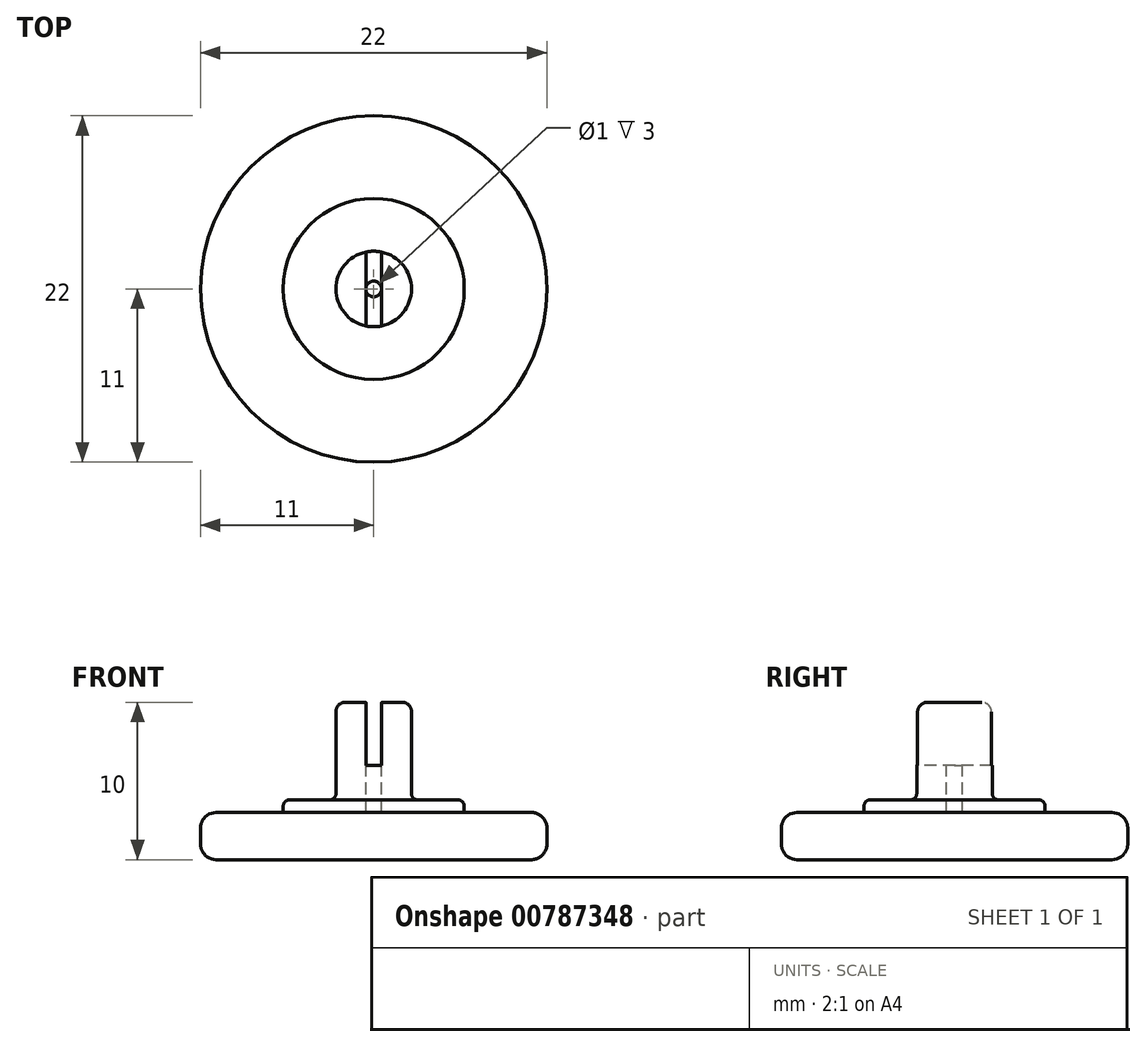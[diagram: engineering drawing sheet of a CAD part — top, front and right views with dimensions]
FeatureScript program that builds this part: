
annotation { "Feature Type Name" : "Feature", "Feature Type Description" : "" }
export const myFeature = defineFeature(function(context is Context, id is Id, definition is map)
    precondition{}
    {
        {
            var Q0;
            Q0=qCreatedBy(makeId("Top.planeOp"),FACE);
            var sketch = newSketch(context, id + "F0", { "sketchPlane" : qUnion([Q0])});
            skCircle(sketch, "E0", {"center": v(0, 0) * mm, "radius": 11 * mm});
            skSolve(sketch);
        }
        {
            var Q0;
            Q0=qSketchRegion(id+"F0",true);
            extrude(context, id + "F1", {"entities" : qUnion([Q0]), "depth" : 3 * mm});
        }
        {
            var Q0;
            Q0=makeQuery(id+"F1.opExtrude","CAP_FACE",FACE,{"disambiguationData":[OSD([sQuery(id+"F0.wireOp",EDGE,"E0")])],"isStart":false});
            var sketch = newSketch(context, id + "F2", { "sketchPlane" : qUnion([Q0])});
            skCircle(sketch, "E1", {"center": v(0, 0) * mm, "radius": 5.75 * mm});
            skSolve(sketch);
        }
        {
            var Q0;
            Q0=qSketchRegion(id+"F2",true);
            extrude(context, id + "F3", {"entities" : qUnion([Q0]), "operationType" : NewBodyOperationType.ADD, "depth" : .8 * mm, "offsetDistance" : 25 * mm});
        }
        {
            var Q0;
            Q0=makeQuery(id+"F3.opExtrude","CAP_FACE",FACE,{"disambiguationData":[OSD([sQuery(id+"F2.wireOp",EDGE,"E1")])],"isStart":false});
            var sketch = newSketch(context, id + "F4", { "sketchPlane" : qUnion([Q0])});
            skCircle(sketch, "E2", {"center": v(0, 0) * mm, "radius": 2.4 * mm});
            skSolve(sketch);
        }
        {
            var Q0;
            Q0=qSketchRegion(id+"F4",true);
            extrude(context, id + "F5", {"entities" : qUnion([Q0]), "operationType" : NewBodyOperationType.ADD, "offsetDistance" : 25 * mm, "depth" : 6.2 * mm});
        }
        {
            var Q0;
            Q0=makeQuery(id+"F5.opExtrude","CAP_FACE",FACE,{"disambiguationData":[OSD([sQuery(id+"F4.wireOp",EDGE,"E2")])],"isStart":false});
            var sketch = newSketch(context, id + "F6", { "sketchPlane" : qUnion([Q0])});
            skCircle(sketch, "E3", {"center": v(0, 0) * mm, "radius": 0.5 * mm});
            skSolve(sketch);
        }
        {
            var Q0;
            Q0=makeQuery(id+"F3.opExtrude","CAP_FACE",FACE,{"disambiguationData":[OSD([sQuery(id+"F2.wireOp",EDGE,"E1")])],"isStart":false});
            cPlane(context, id + "F7", {"entities" : qUnion([Q0]), "cplaneType" : CPlaneType.OFFSET, "offset" : 6 * mm, "width" : 152.4 * mm, "height" : 152.4 * mm});
        }
        {
            var Q0;
            Q0=qCreatedBy(id+"F7.planeOp",FACE);
            var sketch = newSketch(context, id + "F8", { "sketchPlane" : qUnion([Q0])});
            skCircle(sketch, "E4", {"center": v(0, 0) * mm, "radius": 2 * mm});
            skCircle(sketch, "E5", {"center": v(0, 0) * mm, "radius": 2.2 * mm});
            skSolve(sketch);
        }
        {
            var Q0;
            Q0=qSketchRegion(id+"F6",true);
            extrude(context, id + "F9", {"entities" : qUnion([Q0]), "operationType" : NewBodyOperationType.REMOVE, "oppositeDirection" : true, "depth" : 7 * mm});
        }
        {
            var Q0;
            Q0=makeQuery(id+"F5.opExtrude","CAP_FACE",FACE,{"disambiguationData":[OSD([sQuery(id+"F4.wireOp",EDGE,"E2")])],"isStart":false});
            var sketch = newSketch(context, id + "F10", { "sketchPlane" : qUnion([Q0])});
            skLineSegment(sketch, "E6.bottom", {"start": v(-0.5, 4.29) * mm, "end": v(0.5, 4.29) * mm});
            skLineSegment(sketch, "E6.top", {"start": v(-0.5, -4.29) * mm, "end": v(0.5, -4.29) * mm});
            skLineSegment(sketch, "E6.left", {"start": v(-0.5, 4.29) * mm, "end": v(-0.5, -4.29) * mm});
            skLineSegment(sketch, "E6.right", {"start": v(0.5, 4.29) * mm, "end": v(0.5, -4.29) * mm});
            skPoint(sketch, "E6.middle", {"position": v(0, 0) * mm});
            skSolve(sketch);
        }
        {
            var Q0;
            Q0=qSketchRegion(id+"F10",true);
            extrude(context, id + "F11", {"entities" : qUnion([Q0]), "operationType" : NewBodyOperationType.REMOVE, "oppositeDirection" : true, "offsetDistance" : 25 * mm, "depth" : 4 * mm});
        }
        {
            var Q0;
            {var subQ0=sQuery(id+"F4.wireOp",EDGE,"E2");Q0=makeQuery(id+"F11.boolean.opBoolean","SPLIT",EDGE,{"disambiguationData":[TD([makeQuery(id+"F11.opExtrude","SWEPT_FACE",FACE,{"disambiguationData":[OSD([sQuery(id+"F10.wireOp",EDGE,"E6.left")])]})])],"derivedFrom":makeQuery(id+"F5.opExtrude","CAP_EDGE",EDGE,{"disambiguationData":[OSD([subQ0])],"isStart":false})});}
            var Q1;
            {var subQ0=sQuery(id+"F4.wireOp",EDGE,"E2");Q1=makeQuery(id+"F11.boolean.opBoolean","SPLIT",EDGE,{"disambiguationData":[TD([makeQuery(id+"F11.opExtrude","SWEPT_FACE",FACE,{"disambiguationData":[OSD([sQuery(id+"F10.wireOp",EDGE,"E6.right")])]})])],"derivedFrom":makeQuery(id+"F5.opExtrude","CAP_EDGE",EDGE,{"disambiguationData":[OSD([subQ0])],"isStart":false})});}
            fillet(context, id + "F12", {"entities" : qUnion([Q0, Q1]), "radius" : .6 * mm, "tangentPropagation" : true, "allowEdgeOverflow" : false});
        }
        {
            var Q0;
            Q0=makeQuery(id+"F1.opExtrude","CAP_EDGE",EDGE,{"disambiguationData":[OSD([sQuery(id+"F0.wireOp",EDGE,"E0")])],"isStart":false});
            var Q1;
            Q1=makeQuery(id+"F1.opExtrude","CAP_EDGE",EDGE,{"disambiguationData":[OSD([sQuery(id+"F0.wireOp",EDGE,"E0")])],"isStart":true});
            fillet(context, id + "F13", {"entities" : qUnion([Q0, Q1]), "radius" : 1 * mm, "tangentPropagation" : true, "allowEdgeOverflow" : false});
        }
        {
            var Q0;
            Q0=makeQuery(id+"F3.opExtrude","CAP_FACE",FACE,{"disambiguationData":[OSD([sQuery(id+"F2.wireOp",EDGE,"E1")])],"isStart":false});
            fillet(context, id + "F14", {"entities" : qUnion([Q0]), "radius" : 0.4 * mm, "tangentPropagation" : true, "allowEdgeOverflow" : false});
        }
    });
